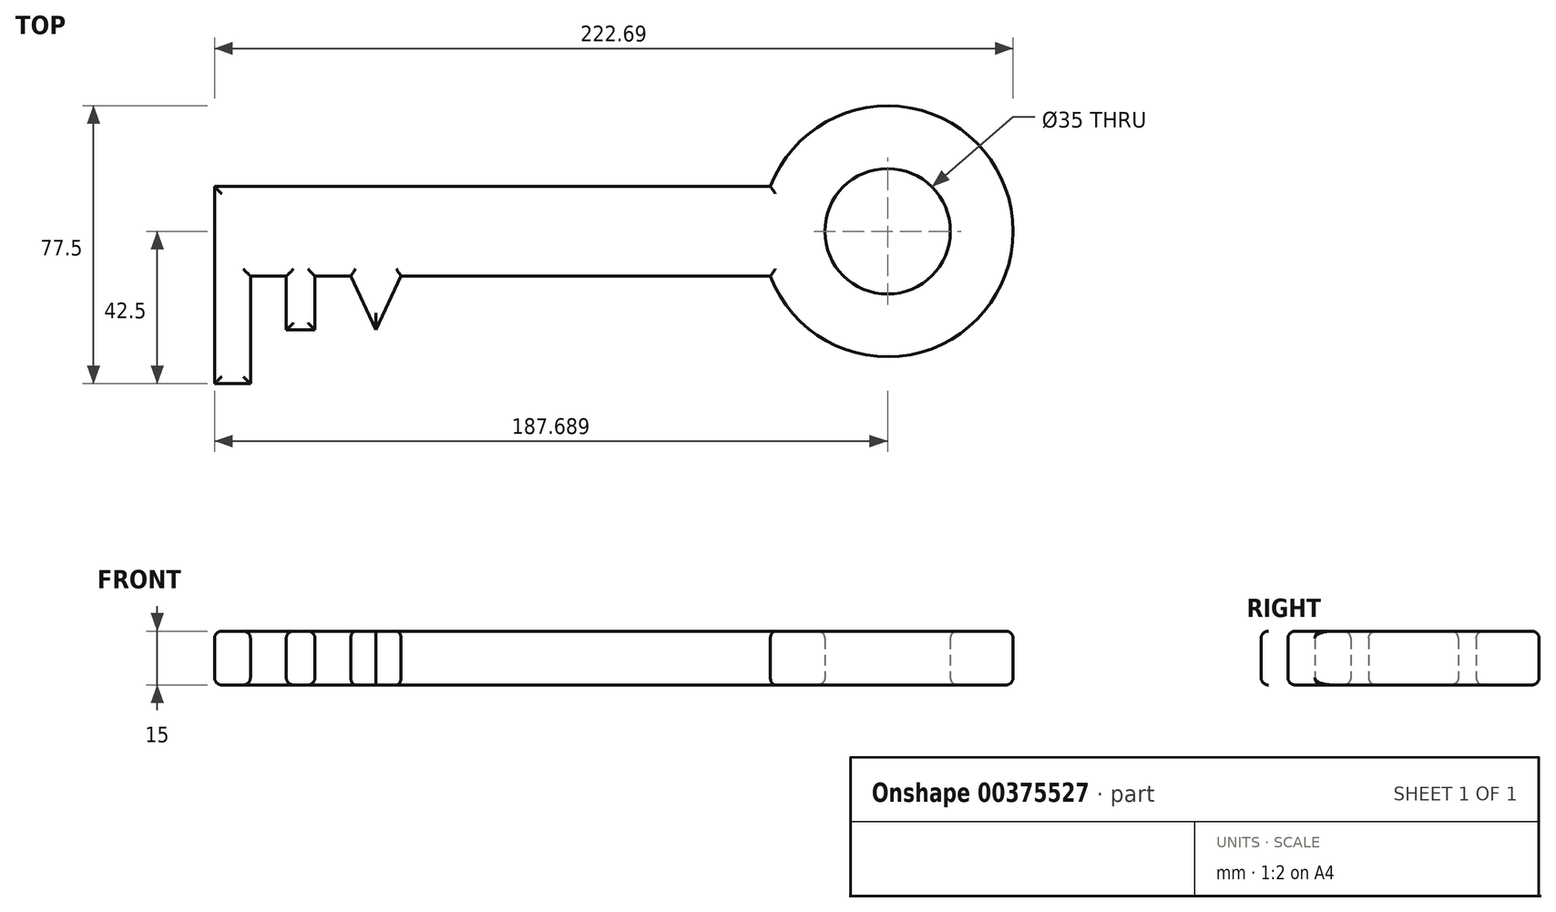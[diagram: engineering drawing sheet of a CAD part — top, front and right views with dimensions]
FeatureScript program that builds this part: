
annotation { "Feature Type Name" : "Feature", "Feature Type Description" : "" }
export const myFeature = defineFeature(function(context is Context, id is Id, definition is map)
    precondition{}
    {
        {
            var Q0;
            Q0=qCreatedBy(makeId("Top.planeOp"),FACE);
            var sketch = newSketch(context, id + "F0", { "sketchPlane" : qUnion([Q0])});
            skLineSegment(sketch, "E0.bottom", {"start": v(-4.9, 40) * mm, "end": v(-159.9, 40) * mm});
            skLineSegment(sketch, "E0.top", {"start": v(-4.9, 15) * mm, "end": v(-159.9, 15) * mm});
            skLineSegment(sketch, "E0.left", {"start": v(-4.9, 40) * mm, "end": v(-4.9, 15) * mm});
            skLineSegment(sketch, "E0.right", {"start": v(-159.9, 40) * mm, "end": v(-159.9, 15) * mm});
            skLineSegment(sketch, "E1.bottom", {"start": v(-159.9, 15) * mm, "end": v(-149.9, 15) * mm});
            skLineSegment(sketch, "E1.top", {"start": v(-159.9, -15) * mm, "end": v(-149.9, -15) * mm});
            skLineSegment(sketch, "E1.left", {"start": v(-159.9, 15) * mm, "end": v(-159.9, -15) * mm});
            skLineSegment(sketch, "E1.right", {"start": v(-149.9, 15) * mm, "end": v(-149.9, -15) * mm});
            skLineSegment(sketch, "E2.bottom", {"start": v(-139.9, 15) * mm, "end": v(-131.9, 15) * mm});
            skLineSegment(sketch, "E2.top", {"start": v(-139.9, 0) * mm, "end": v(-131.9, 0) * mm});
            skLineSegment(sketch, "E2.left", {"start": v(-139.9, 15) * mm, "end": v(-139.9, 0) * mm});
            skLineSegment(sketch, "E2.right", {"start": v(-131.9, 15) * mm, "end": v(-131.9, 0) * mm});
            skLineSegment(sketch, "E3", {"start": v(-121.9, 15) * mm, "end": v(-114.9, 0) * mm});
            skLineSegment(sketch, "E4", {"start": v(-114.9, 0) * mm, "end": v(-107.9, 15) * mm});
            skArc(sketch, "E5", {"start": v(-4.9, 15) * mm, "mid": v(62.8, 27.5) * mm, "end": v(-4.9, 40) * mm});
            skCircle(sketch, "E6", {"center": v(27.8, 27.5) * mm, "radius": 17.5 * mm});
            skLineSegment(sketch, "E7", {"start": v(-159.9, 27.5) * mm, "end": v(27.8, 27.5) * mm, "construction": true});
            skSolve(sketch);
        }
        {
            var Q0;
            Q0 = qSketchRegion(id + "F0", true);
            extrude(context, id + "F1", {"entities" : qUnion([Q0]), "depth" : 15 * mm});
        }
        {
            var Q0;
            Q0=makeQuery(id+"F1.opExtrude","CAP_EDGE",EDGE,{"disambiguationData":[OSD([sQuery(id+"F0.wireOp",EDGE,"E5")])],"isStart":false});
            var Q1;
            Q1=makeQuery(id+"F1.opExtrude","CAP_EDGE",EDGE,{"disambiguationData":[OSD([sQuery(id+"F0.wireOp",EDGE,"E0.bottom")])],"isStart":false});
            var Q2;
            Q2=makeQuery(id+"F1.opExtrude","CAP_EDGE",EDGE,{"disambiguationData":[OSD([sQuery(id+"F0.wireOp",EDGE,"E6")])],"isStart":false});
            var Q3;
            {var subQ0=sQuery(id+"F0.wireOp",EDGE,"E0.top");Q3=makeQuery(id+"F1.opExtrude","CAP_EDGE",EDGE,{"disambiguationData":[OSD([subQ0]),TDD([makeQuery(id+"F0.imprint","IMPRINT",EDGE,{"disambiguationData":[TD([[makeQuery(id+"F0.imprint","INTERSECT",VERTEX,{"derivedFrom":[subQ0,sQuery(id+"F0.wireOp",EDGE,"E4")]}),1.0]])],"derivedFrom":subQ0})])],"isStart":false});}
            var Q4;
            Q4=makeQuery(id+"F1.opExtrude","CAP_EDGE",EDGE,{"disambiguationData":[OSD([sQuery(id+"F0.wireOp",EDGE,"E4")])],"isStart":false});
            var Q5;
            Q5=makeQuery(id+"F1.opExtrude","CAP_EDGE",EDGE,{"disambiguationData":[OSD([sQuery(id+"F0.wireOp",EDGE,"E2.right")])],"isStart":false});
            var Q6;
            Q6=makeQuery(id+"F1.opExtrude","CAP_EDGE",EDGE,{"disambiguationData":[OSD([sQuery(id+"F0.wireOp",EDGE,"E3")])],"isStart":false});
            var Q7;
            {var subQ0=sQuery(id+"F0.wireOp",EDGE,"E0.top");Q7=makeQuery(id+"F1.opExtrude","CAP_EDGE",EDGE,{"disambiguationData":[OSD([subQ0]),TDD([makeQuery(id+"F0.imprint","IMPRINT",EDGE,{"disambiguationData":[TD([[makeQuery(id+"F0.imprint","INTERSECT",VERTEX,{"derivedFrom":[subQ0,sQuery(id+"F0.wireOp",EDGE,"E3")]}),-1.0]])],"derivedFrom":subQ0})])],"isStart":false});}
            var Q8;
            Q8=makeQuery(id+"F1.opExtrude","CAP_EDGE",EDGE,{"disambiguationData":[OSD([sQuery(id+"F0.wireOp",EDGE,"E1.right")])],"isStart":false});
            var Q9;
            {var subQ0=sQuery(id+"F0.wireOp",EDGE,"E0.top");Q9=makeQuery(id+"F1.opExtrude","CAP_EDGE",EDGE,{"disambiguationData":[OSD([subQ0]),TDD([makeQuery(id+"F0.imprint","IMPRINT",EDGE,{"disambiguationData":[TD([[makeQuery(id+"F0.imprint","INTERSECT",VERTEX,{"derivedFrom":[subQ0,sQuery(id+"F0.wireOp",EDGE,"E1.bottom"),sQuery(id+"F0.wireOp",EDGE,"E1.right")]}),1.0]])],"derivedFrom":subQ0})])],"isStart":false});}
            var Q10;
            Q10=makeQuery(id+"F1.opExtrude","CAP_EDGE",EDGE,{"disambiguationData":[OSD([sQuery(id+"F0.wireOp",EDGE,"E2.left")])],"isStart":false});
            var Q11;
            Q11=makeQuery(id+"F1.opExtrude","CAP_EDGE",EDGE,{"disambiguationData":[OSD([sQuery(id+"F0.wireOp",EDGE,"E0.right"),sQuery(id+"F0.wireOp",EDGE,"E1.left")])],"isStart":false});
            var Q12;
            Q12=makeQuery(id+"F1.opExtrude","CAP_EDGE",EDGE,{"disambiguationData":[OSD([sQuery(id+"F0.wireOp",EDGE,"E1.top")])],"isStart":false});
            var Q13;
            Q13=makeQuery(id+"F1.opExtrude","CAP_EDGE",EDGE,{"disambiguationData":[OSD([sQuery(id+"F0.wireOp",EDGE,"E2.top")])],"isStart":false});
            var Q14;
            Q14=makeQuery(id+"F1.opExtrude","CAP_EDGE",EDGE,{"disambiguationData":[OSD([sQuery(id+"F0.wireOp",EDGE,"E5")])],"isStart":true});
            var Q15;
            Q15=makeQuery(id+"F1.opExtrude","CAP_EDGE",EDGE,{"disambiguationData":[OSD([sQuery(id+"F0.wireOp",EDGE,"E6")])],"isStart":true});
            var Q16;
            {var subQ0=sQuery(id+"F0.wireOp",EDGE,"E0.top");Q16=makeQuery(id+"F1.opExtrude","CAP_EDGE",EDGE,{"disambiguationData":[OSD([subQ0]),TDD([makeQuery(id+"F0.imprint","IMPRINT",EDGE,{"disambiguationData":[TD([[makeQuery(id+"F0.imprint","INTERSECT",VERTEX,{"derivedFrom":[subQ0,sQuery(id+"F0.wireOp",EDGE,"E4")]}),1.0]])],"derivedFrom":subQ0})])],"isStart":true});}
            var Q17;
            Q17=makeQuery(id+"F1.opExtrude","CAP_EDGE",EDGE,{"disambiguationData":[OSD([sQuery(id+"F0.wireOp",EDGE,"E0.bottom")])],"isStart":true});
            var Q18;
            {var subQ0=sQuery(id+"F0.wireOp",EDGE,"E0.top");Q18=makeQuery(id+"F1.opExtrude","CAP_EDGE",EDGE,{"disambiguationData":[OSD([subQ0]),TDD([makeQuery(id+"F0.imprint","IMPRINT",EDGE,{"disambiguationData":[TD([[makeQuery(id+"F0.imprint","INTERSECT",VERTEX,{"derivedFrom":[subQ0,sQuery(id+"F0.wireOp",EDGE,"E3")]}),-1.0]])],"derivedFrom":subQ0})])],"isStart":true});}
            var Q19;
            Q19=makeQuery(id+"F1.opExtrude","CAP_EDGE",EDGE,{"disambiguationData":[OSD([sQuery(id+"F0.wireOp",EDGE,"E3")])],"isStart":true});
            var Q20;
            Q20=makeQuery(id+"F1.opExtrude","CAP_EDGE",EDGE,{"disambiguationData":[OSD([sQuery(id+"F0.wireOp",EDGE,"E2.left")])],"isStart":true});
            var Q21;
            Q21=makeQuery(id+"F1.opExtrude","CAP_EDGE",EDGE,{"disambiguationData":[OSD([sQuery(id+"F0.wireOp",EDGE,"E4")])],"isStart":true});
            var Q22;
            Q22=makeQuery(id+"F1.opExtrude","CAP_EDGE",EDGE,{"disambiguationData":[OSD([sQuery(id+"F0.wireOp",EDGE,"E2.right")])],"isStart":true});
            var Q23;
            Q23=makeQuery(id+"F1.opExtrude","CAP_EDGE",EDGE,{"disambiguationData":[OSD([sQuery(id+"F0.wireOp",EDGE,"E2.top")])],"isStart":true});
            var Q24;
            {var subQ0=sQuery(id+"F0.wireOp",EDGE,"E0.top");Q24=makeQuery(id+"F1.opExtrude","CAP_EDGE",EDGE,{"disambiguationData":[OSD([subQ0]),TDD([makeQuery(id+"F0.imprint","IMPRINT",EDGE,{"disambiguationData":[TD([[makeQuery(id+"F0.imprint","INTERSECT",VERTEX,{"derivedFrom":[subQ0,sQuery(id+"F0.wireOp",EDGE,"E1.bottom"),sQuery(id+"F0.wireOp",EDGE,"E1.right")]}),1.0]])],"derivedFrom":subQ0})])],"isStart":true});}
            var Q25;
            Q25=makeQuery(id+"F1.opExtrude","CAP_EDGE",EDGE,{"disambiguationData":[OSD([sQuery(id+"F0.wireOp",EDGE,"E1.right")])],"isStart":true});
            var Q26;
            Q26=makeQuery(id+"F1.opExtrude","CAP_EDGE",EDGE,{"disambiguationData":[OSD([sQuery(id+"F0.wireOp",EDGE,"E1.top")])],"isStart":true});
            var Q27;
            Q27=makeQuery(id+"F1.opExtrude","CAP_EDGE",EDGE,{"disambiguationData":[OSD([sQuery(id+"F0.wireOp",EDGE,"E0.right"),sQuery(id+"F0.wireOp",EDGE,"E1.left")])],"isStart":true});
            fillet(context, id + "F2", {"entities" : qUnion([Q0, Q1, Q2, Q3, Q4, Q5, Q6, Q7, Q8, Q9, Q10, Q11, Q12, Q13, Q14, Q15, Q16, Q17, Q18, Q19, Q20, Q21, Q22, Q23, Q24, Q25, Q26, Q27]), "radius" : 2 * mm, "tangentPropagation" : true, "allowEdgeOverflow" : false});
        }
    });
